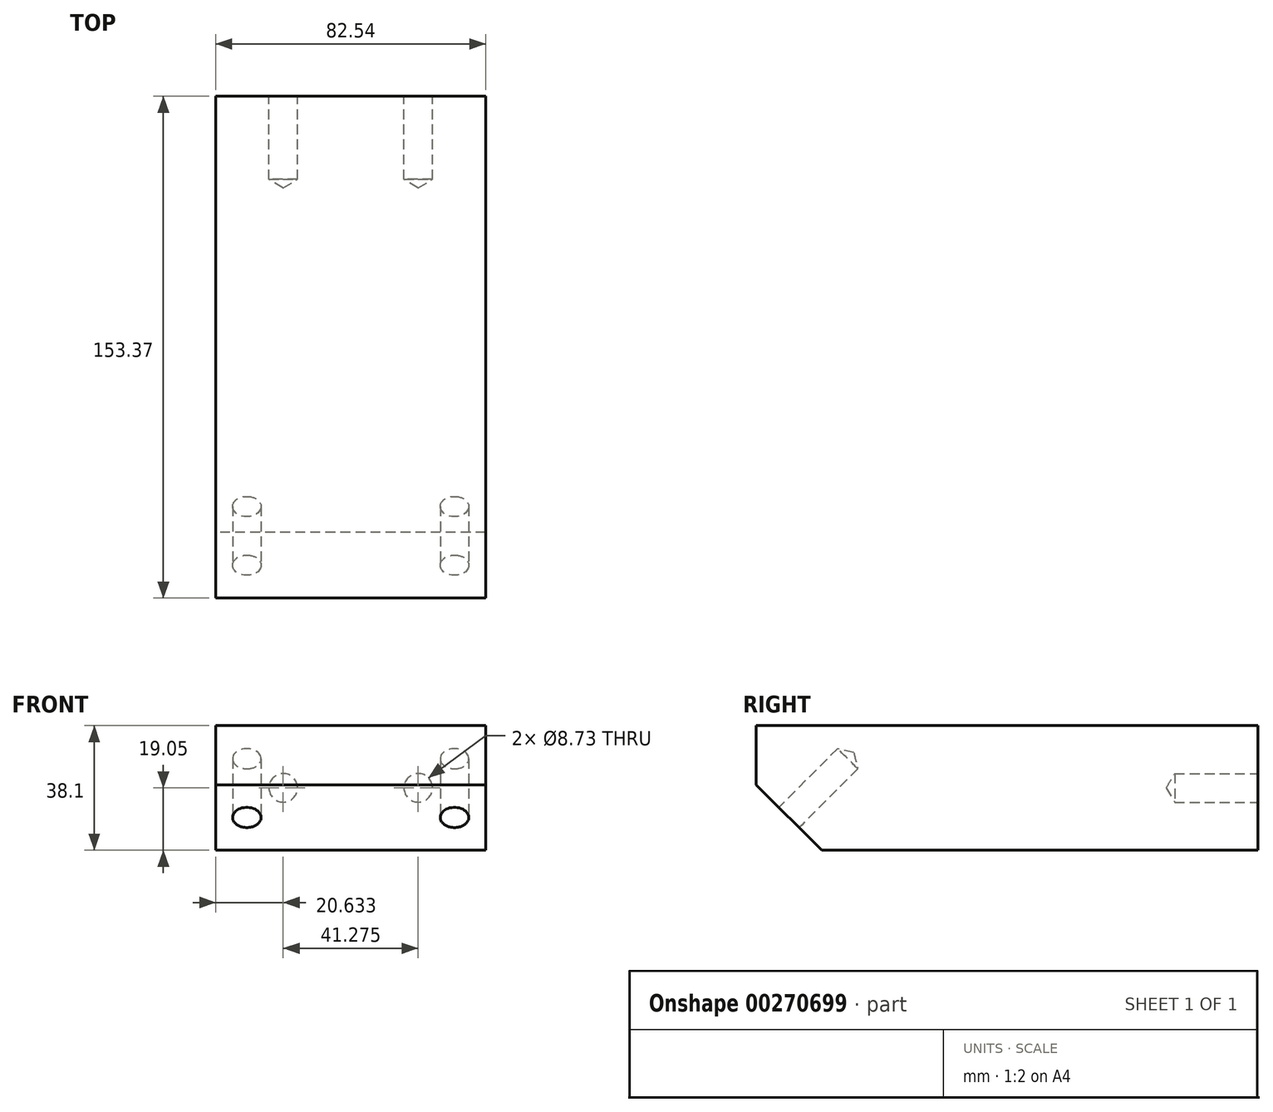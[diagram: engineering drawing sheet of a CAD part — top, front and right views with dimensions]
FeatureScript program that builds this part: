
annotation { "Feature Type Name" : "Feature", "Feature Type Description" : "" }
export const myFeature = defineFeature(function(context is Context, id is Id, definition is map)
    precondition{}
    {
        {
            var Q0;
            Q0=qCreatedBy(makeId("Front.planeOp"),FACE);
            var sketch = newSketch(context, id + "F0", { "sketchPlane" : qUnion([Q0])});
            skLineSegment(sketch, "E0.bottom", {"start": v(41.28, 19.05) * mm, "end": v(-41.28, 19.05) * mm});
            skLineSegment(sketch, "E0.top", {"start": v(41.28, -19.05) * mm, "end": v(-41.28, -19.05) * mm});
            skLineSegment(sketch, "E0.left", {"start": v(41.28, 19.05) * mm, "end": v(41.28, -19.05) * mm});
            skLineSegment(sketch, "E0.right", {"start": v(-41.28, 19.05) * mm, "end": v(-41.28, -19.05) * mm});
            skPoint(sketch, "E0.middle", {"position": v(0, 0) * mm});
            skSolve(sketch);
        }
        {
            var Q0;
            Q0 = qSketchRegion(id + "F0", true);
            extrude(context, id + "F1", {"entities" : qUnion([Q0]), "depth" : 153.37 * mm});
        }
        {
            var Q0;
            Q0=makeQuery(id+"F1.opExtrude","CAP_EDGE",EDGE,{"disambiguationData":[OSD([sQuery(id+"F0.wireOp",EDGE,"E0.top")])],"isStart":false});
            chamfer(context, id + "F2", {"entities" : qUnion([Q0]), "chamferType" : ChamferType.OFFSET_ANGLE, "width" : 20.02 * mm, "oppositeDirection" : false, "angle" : 45 * degree, "tangentPropagation" : true});
        }
        {
            var Q0;
            Q0=makeQuery(id+"F2.opChamfer","BLEND_FACE",FACE,{"disambiguationData":[OSD([sQuery(id+"F0.wireOp",EDGE,"E0.top")])]});
            var sketch = newSketch(context, id + "F3", { "sketchPlane" : qUnion([Q0])});
            skCircle(sketch, "E1", {"center": v(-31.75, 94.98) * mm, "radius": 4.36 * mm});
            skCircle(sketch, "E2", {"center": v(31.75, 94.98) * mm, "radius": 4.36 * mm});
            skSolve(sketch);
        }
        {
            var Q0;
            Q0=makeQuery(id+"F1.opExtrude","CAP_FACE",FACE,{"disambiguationData":[OSD([sQuery(id+"F0.wireOp",EDGE,"E0.bottom"),sQuery(id+"F0.wireOp",EDGE,"E0.top"),sQuery(id+"F0.wireOp",EDGE,"E0.left"),sQuery(id+"F0.wireOp",EDGE,"E0.right")])],"isStart":true});
            var sketch = newSketch(context, id + "F4", { "sketchPlane" : qUnion([Q0])});
            skPoint(sketch, "E3", {"position": v(-20.64, 0) * mm});
            skPoint(sketch, "E4", {"position": v(20.64, 0) * mm});
            skSolve(sketch);
        }
        {
            var Q0;
            Q0=sQuery(id+"F3.wireOp",VERTEX,"E1.center");
            var Q1;
            Q1=sQuery(id+"F3.wireOp",VERTEX,"E2.center");
            var Q2;
            Q2=sQuery(id+"F4.wireOp",VERTEX,"E3");
            var Q3;
            Q3=sQuery(id+"F4.wireOp",VERTEX,"E4");
            var Q4;
            Q4=makeQuery(id+"F1.opExtrude","SWEPT_BODY",BODY,{"disambiguationData":[OSD([sQuery(id+"F0.wireOp",EDGE,"E0.bottom"),sQuery(id+"F0.wireOp",EDGE,"E0.top"),sQuery(id+"F0.wireOp",EDGE,"E0.left"),sQuery(id+"F0.wireOp",EDGE,"E0.right")])]});
            hole(context, id + "F5", {"style" : HoleStyle.SIMPLE, "endStyle" : HoleEndStyle.BLIND, "holeDiameter" : 8.73 * mm, "holeDepth" : 25.4 * mm, "tappedDepth" : 12.7 * mm, "tapClearance" : 3, "locations" : qUnion([Q0, Q1, Q2, Q3]), "scope" : qUnion([Q4])});
        }
    });
